# Revit family: SCB435-KT
name_source: partatom
category: Detail Items
revit_build: Autodesk Revit 2015 (Build: 20140606_1530(x64)
units: mm (PartAtom-declared; Revit-internal decimal feet)

## types (4) — shared parameters
Density = 0.16 kg
Description = Connector Other
EPD = https://www.strongtie.eu
ETA / DoP = https://www.strongtie.eu
Manufacturer = Simpson Strong-Tie
Model = SCB43.5-KT
Model Disclaimer = Contact Simpson Strong-Tie Company  for more information
Model ID = 0160950337429114291552118862626552721359
Name = SCB43.5-KT
ObjectType = SCB43.5-KT
Product Material = Galvanised
Product Type = Connector Other
Reference = SCB43.5-KT
Technical datasheet = https://www.strongtie.eu
URL = www.strongtie.eu
UniClass Number = Pr_20_29_31_13
UniClass Title = Carbon steel punched metal plate fasteners

## per-type parameters (varying)
| type | _visiblefront | _visibleleft | _visibleright | _visibletop |
| SST_SCB43.5-KT_Front | Yes | No | No | No |
| SST_SCB43.5-KT_Top | No | No | No | Yes |
| SST_SCB43.5-KT_Left | No | Yes | No | No |
| SST_SCB43.5-KT_Right | No | No | Yes | No |

## geometry (parser evidence)
native form markers: Blend x2, Sweep x1
no freeform markers — native parametric forms only
